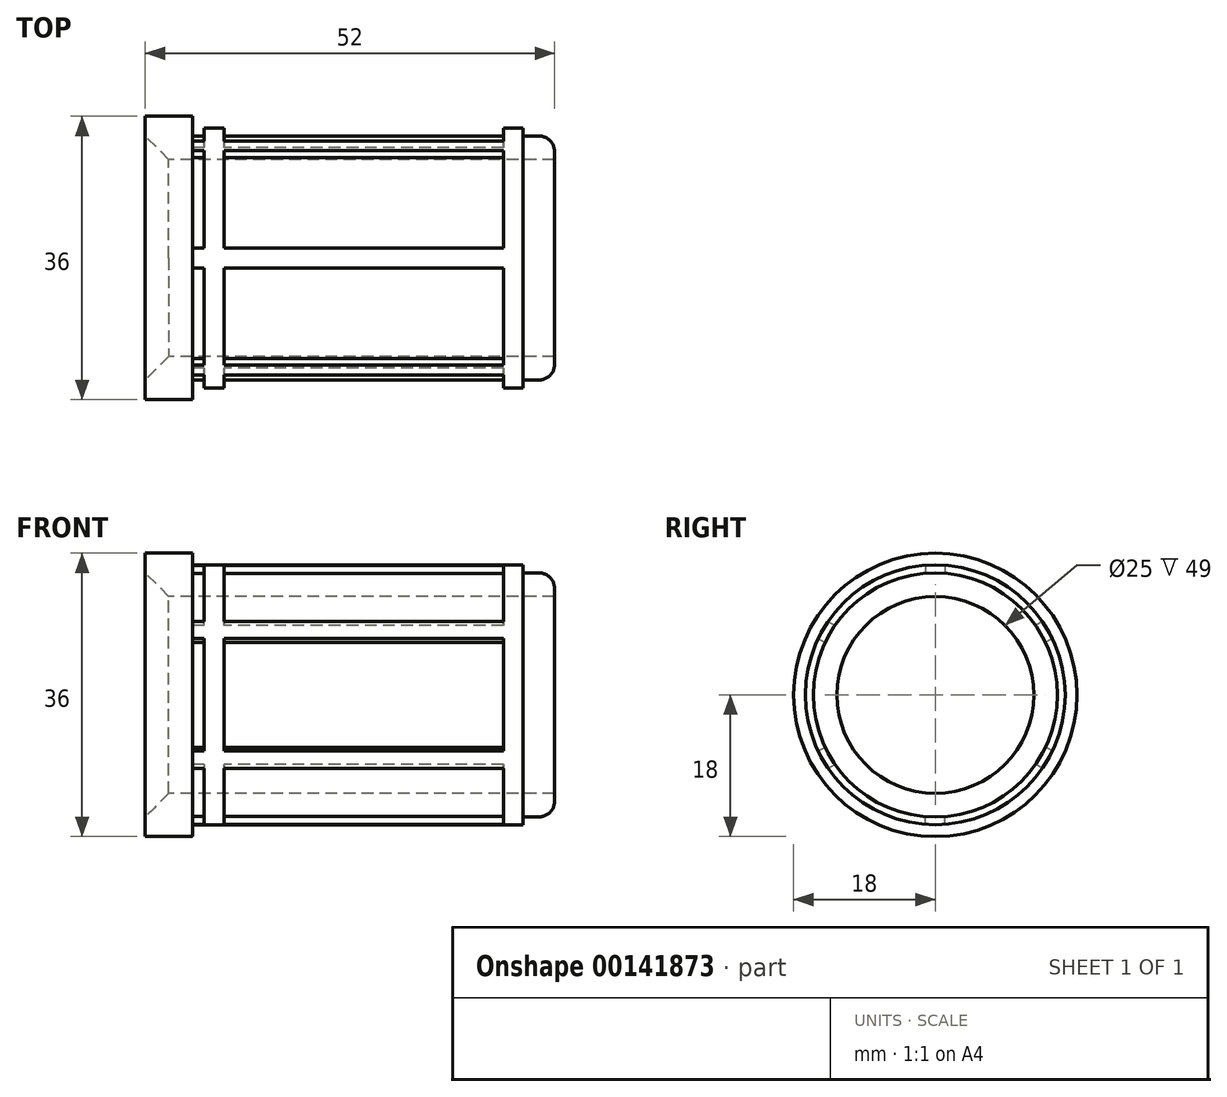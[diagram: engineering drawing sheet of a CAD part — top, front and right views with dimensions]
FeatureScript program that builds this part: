
annotation { "Feature Type Name" : "Feature", "Feature Type Description" : "" }
export const myFeature = defineFeature(function(context is Context, id is Id, definition is map)
    precondition{}
    {
        {
            var Q0;
            Q0=qCreatedBy(makeId("Top.planeOp"),FACE);
            var sketch = newSketch(context, id + "F0", { "sketchPlane" : qUnion([Q0])});
            skLineSegment(sketch, "E0", {"start": v(0, 12.5) * mm, "end": v(52, 12.5) * mm});
            skLineSegment(sketch, "E1", {"start": v(52, 12.5) * mm, "end": v(52, 13.5) * mm});
            skLineSegment(sketch, "E2", {"start": v(50, 15.5) * mm, "end": v(48, 15.5) * mm});
            skLineSegment(sketch, "E3", {"start": v(6, 15.5) * mm, "end": v(6, 18) * mm});
            skLineSegment(sketch, "E4", {"start": v(6, 18) * mm, "end": v(0, 18) * mm});
            skLineSegment(sketch, "E5", {"start": v(0, 18) * mm, "end": v(0, 12.5) * mm});
            skPoint(sketch, "E6.visualSharp", {"position": v(52, 15.5) * mm});
            skArc(sketch, "E6.filletArc", {"start": v(52, 13.5) * mm, "mid": v(51.41, 14.91) * mm, "end": v(50, 15.5) * mm});
            skLineSegment(sketch, "E7", {"start": v(0, 0) * mm, "end": v(59.42, 0) * mm, "construction": true});
            skLineSegment(sketch, "E8", {"start": v(7.5, 15.5) * mm, "end": v(7.5, 16.5) * mm});
            skLineSegment(sketch, "E9", {"start": v(7.5, 16.5) * mm, "end": v(10, 16.5) * mm});
            skLineSegment(sketch, "E10", {"start": v(10, 16.5) * mm, "end": v(10, 15.5) * mm});
            skLineSegment(sketch, "E11", {"start": v(45.5, 15.5) * mm, "end": v(45.5, 16.5) * mm});
            skLineSegment(sketch, "E12", {"start": v(45.5, 16.5) * mm, "end": v(48, 16.5) * mm});
            skLineSegment(sketch, "E13", {"start": v(48, 16.5) * mm, "end": v(48, 15.5) * mm});
            skLineSegment(sketch, "E14.trimOffspring", {"start": v(7.5, 15.5) * mm, "end": v(6, 15.5) * mm});
            skLineSegment(sketch, "E15.trimOffspring", {"start": v(45.5, 15.5) * mm, "end": v(10, 15.5) * mm});
            skSolve(sketch);
        }
        {
            var Q0;
            Q0 = qSketchRegion(id + "F0", true);
            var Q1;
            Q1=sQuery(id+"F0.wireOp",EDGE,"E7");
            var Q2;
            Q2=sQuery(id+"F0.wireOp",EDGE,"E7");
            revolve(context, id + "F1", {"entities" : qUnion([Q0]), "surfaceEntities" : qUnion([Q1]), "axis" : qUnion([Q2]), "revolveType" : RevolveType.FULL});
        }
        {
            var Q0;
            Q0=makeQuery(id+"F1.opRevolve","SWEPT_FACE",FACE,{"disambiguationData":[OSD([sQuery(id+"F0.wireOp",EDGE,"E3")])]});
            var sketch = newSketch(context, id + "F2", { "sketchPlane" : qUnion([Q0])});
            skCircle(sketch, "E16.0", {"center": v(0, 0) * mm, "radius": 18 * mm, "construction": true});
            skArc(sketch, "E17.0", {"start": v(1.25, 15.45) * mm, "mid": v(0, 15.5) * mm, "end": v(-1.25, 15.45) * mm});
            skArc(sketch, "E18.0", {"start": v(1.25, 16.45) * mm, "mid": v(0, 16.5) * mm, "end": v(-1.25, 16.45) * mm});
            skLineSegment(sketch, "E19", {"start": v(0, 15.5) * mm, "end": v(0, 16.5) * mm});
            skLineSegment(sketch, "E20.0", {"start": v(1.25, 15.45) * mm, "end": v(1.25, 16.45) * mm});
            skLineSegment(sketch, "E21.0", {"start": v(0, 15.5) * mm, "end": v(0, 16.5) * mm, "construction": true});
            skLineSegment(sketch, "E22.MirrorCS", {"start": v(-1.25, 15.45) * mm, "end": v(-1.25, 16.45) * mm});
            skPoint(sketch, "E23.orphan", {"position": v(-1.25, 15.45) * mm});
            skArc(sketch, "E24.1.0", {"start": v(-12.75, 8.8) * mm, "mid": v(-13.42, 7.75) * mm, "end": v(-14, 6.64) * mm});
            skLineSegment(sketch, "E24.1.1", {"start": v(-12.75, 8.8) * mm, "end": v(-13.62, 9.3) * mm});
            skArc(sketch, "E24.1.2", {"start": v(-13.62, 9.3) * mm, "mid": v(-14.3, 8.25) * mm, "end": v(-14.87, 7.14) * mm});
            skLineSegment(sketch, "E24.1.3", {"start": v(-14, 6.64) * mm, "end": v(-14.87, 7.14) * mm});
            skArc(sketch, "E24.2.0", {"start": v(-14, -6.64) * mm, "mid": v(-13.42, -7.75) * mm, "end": v(-12.75, -8.8) * mm});
            skLineSegment(sketch, "E24.2.1", {"start": v(-14, -6.64) * mm, "end": v(-14.87, -7.14) * mm});
            skArc(sketch, "E24.2.2", {"start": v(-14.87, -7.14) * mm, "mid": v(-14.29, -8.25) * mm, "end": v(-13.62, -9.31) * mm});
            skLineSegment(sketch, "E24.2.3", {"start": v(-12.75, -8.8) * mm, "end": v(-13.62, -9.31) * mm});
            skArc(sketch, "E24.3.0", {"start": v(-1.25, -15.45) * mm, "mid": v(0, -15.5) * mm, "end": v(1.25, -15.45) * mm});
            skLineSegment(sketch, "E24.3.1", {"start": v(-1.25, -15.45) * mm, "end": v(-1.25, -16.45) * mm});
            skArc(sketch, "E24.3.2", {"start": v(-1.25, -16.45) * mm, "mid": v(0, -16.5) * mm, "end": v(1.25, -16.45) * mm});
            skLineSegment(sketch, "E24.3.3", {"start": v(1.25, -15.45) * mm, "end": v(1.25, -16.45) * mm});
            skArc(sketch, "E24.4.0", {"start": v(12.75, -8.8) * mm, "mid": v(13.42, -7.75) * mm, "end": v(14, -6.64) * mm});
            skLineSegment(sketch, "E24.4.1", {"start": v(12.75, -8.8) * mm, "end": v(13.62, -9.3) * mm});
            skArc(sketch, "E24.4.2", {"start": v(13.62, -9.3) * mm, "mid": v(14.3, -8.25) * mm, "end": v(14.87, -7.14) * mm});
            skLineSegment(sketch, "E24.4.3", {"start": v(14, -6.64) * mm, "end": v(14.87, -7.14) * mm});
            skArc(sketch, "E24.5.0", {"start": v(14, 6.64) * mm, "mid": v(13.42, 7.75) * mm, "end": v(12.75, 8.8) * mm});
            skLineSegment(sketch, "E24.5.1", {"start": v(14, 6.64) * mm, "end": v(14.87, 7.14) * mm});
            skArc(sketch, "E24.5.2", {"start": v(14.87, 7.14) * mm, "mid": v(14.29, 8.25) * mm, "end": v(13.62, 9.31) * mm});
            skLineSegment(sketch, "E24.5.3", {"start": v(12.75, 8.8) * mm, "end": v(13.62, 9.31) * mm});
            skSolve(sketch);
        }
        {
            var Q0;
            Q0 = qSketchRegion(id + "F2", true);
            var Q1;
            Q1=makeQuery(id+"F1.opRevolve","SWEPT_FACE",FACE,{"disambiguationData":[OSD([sQuery(id+"F0.wireOp",EDGE,"E11")])]});
            extrude(context, id + "F3", {"entities" : qUnion([Q0]), "operationType" : NewBodyOperationType.ADD, "endBound" : BoundingType.UP_TO_SURFACE, "endBoundEntityFace" : qUnion([Q1]), "depth" : 25 * mm});
        }
        {
            var Q0;
            Q0=makeQuery(id+"F1.opRevolve","SWEPT_EDGE",EDGE,{"disambiguationData":[OSD([sQuery(id+"F0.wireOp",EDGE,"E0"),sQuery(id+"F0.wireOp",EDGE,"E5")])]});
            chamfer(context, id + "F4", {"entities" : qUnion([Q0]), "width" : 3 * mm, "tangentPropagation" : true});
        }
    });
